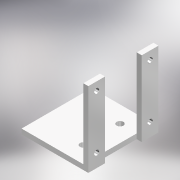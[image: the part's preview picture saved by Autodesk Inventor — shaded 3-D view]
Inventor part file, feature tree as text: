
AUTODESK INVENTOR PART (.ipt)
format: ipt  version: 2021 (Build 250183000, 183)  size: 159,744 bytes
history: native  units: mm
features: sketch x5, extrude x4, mirror x1, thicken_offset x1
ambient origin geometry x8: Origin, YZ Plane, XZ Plane, XY Plane, X Axis, Y Axis, Z Axis, Center Point
bodies: Solid1 (feature_tree)
feature tree (11):
  extrude  "Extrusion1"  Depth=42.0mm
  extrude  "Extrusion2"  Depth=10.0mm
  extrude  "Extrusion3"  Depth=10.0mm
  mirror  "Mirror1"
  extrude  "Extrusion5"  Depth=3.0mm TaperAngle=0.0deg
  sketch  "Sketch6"  dims[d10=3.0mm d11=3.0mm d12=3.0mm d13=0.0mm d18=4.0mm d19=4.0mm d20=3.0mm d21=0.0mm d22=17.0mm d23=17.0mm]
  thicken_offset  "Thicken1"
  sketch  "Sketch1"  dims[d0=20.0mm d1=42.0mm]
  sketch  "Sketch2"  dims[d2=3.0mm d3=0.0mm d4=10.0mm]
  sketch  "Sketch3"  dims[d5=45.0mm d6=10.0mm]
  sketch  "Sketch5"  dims[d7=45.0mm d8=3.0mm d9=0.0mm]
